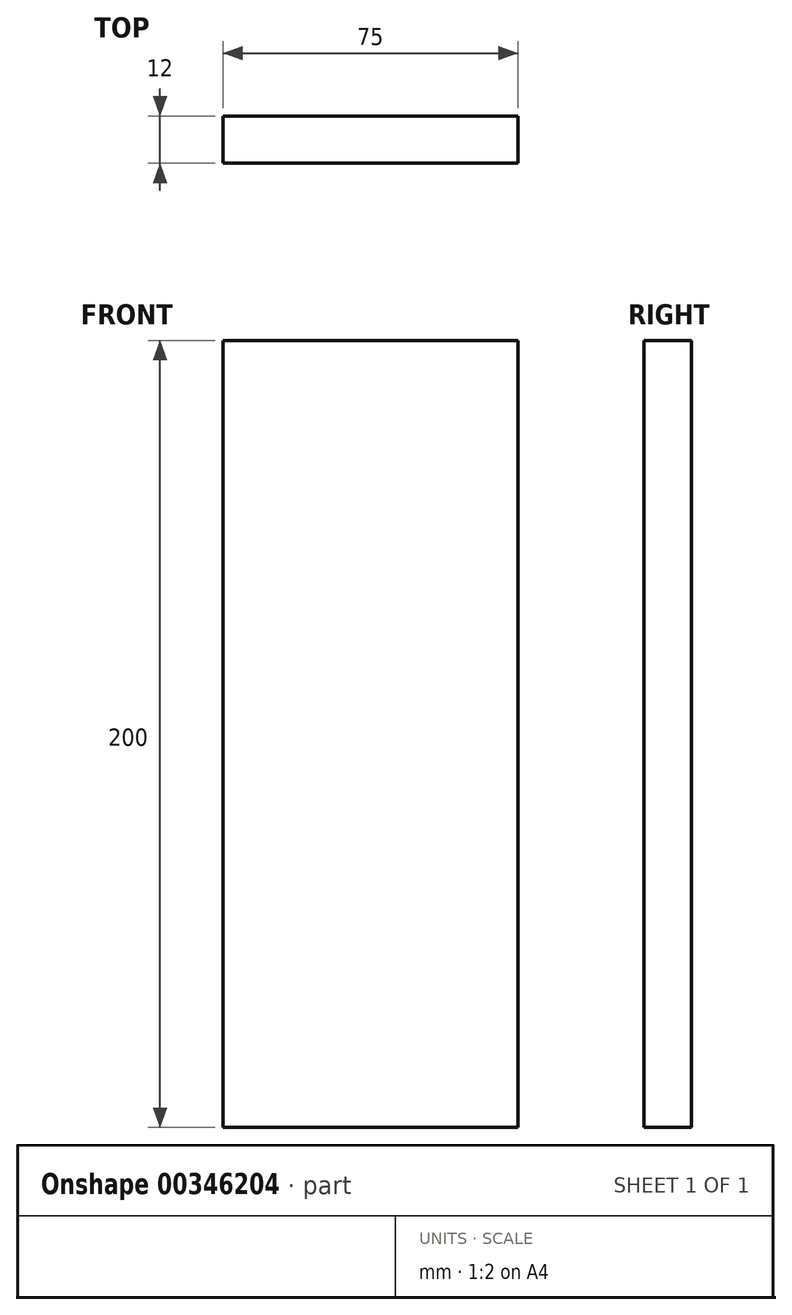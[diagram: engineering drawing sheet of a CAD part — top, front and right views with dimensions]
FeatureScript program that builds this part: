
annotation { "Feature Type Name" : "Feature", "Feature Type Description" : "" }
export const myFeature = defineFeature(function(context is Context, id is Id, definition is map)
    precondition{}
    {
        {
            var Q0;
            Q0=qCreatedBy(makeId("Front.planeOp"),FACE);
            var sketch = newSketch(context, id + "F0", { "sketchPlane" : qUnion([Q0])});
            skLineSegment(sketch, "E0.bottom", {"start": v(-37.5, 100) * mm, "end": v(37.5, 100) * mm});
            skLineSegment(sketch, "E0.top", {"start": v(-37.5, -100) * mm, "end": v(37.5, -100) * mm});
            skLineSegment(sketch, "E0.left", {"start": v(-37.5, 100) * mm, "end": v(-37.5, -100) * mm});
            skLineSegment(sketch, "E0.right", {"start": v(37.5, 100) * mm, "end": v(37.5, -100) * mm});
            skPoint(sketch, "E0.middle", {"position": v(0, 0) * mm});
            skSolve(sketch);
        }
        {
            var Q0;
            Q0=makeQuery(id+"F0.imprint","IMPRINT",FACE,{"disambiguationData":[TD([[makeQuery(id+"F0.imprint","IMPRINT",EDGE,{"derivedFrom":sQuery(id+"F0.wireOp",EDGE,"E0.bottom")}),-1.0]])]});
            extrude(context, id + "F1", {"entities" : qUnion([Q0]), "depth" : 12 * mm});
        }
    });
